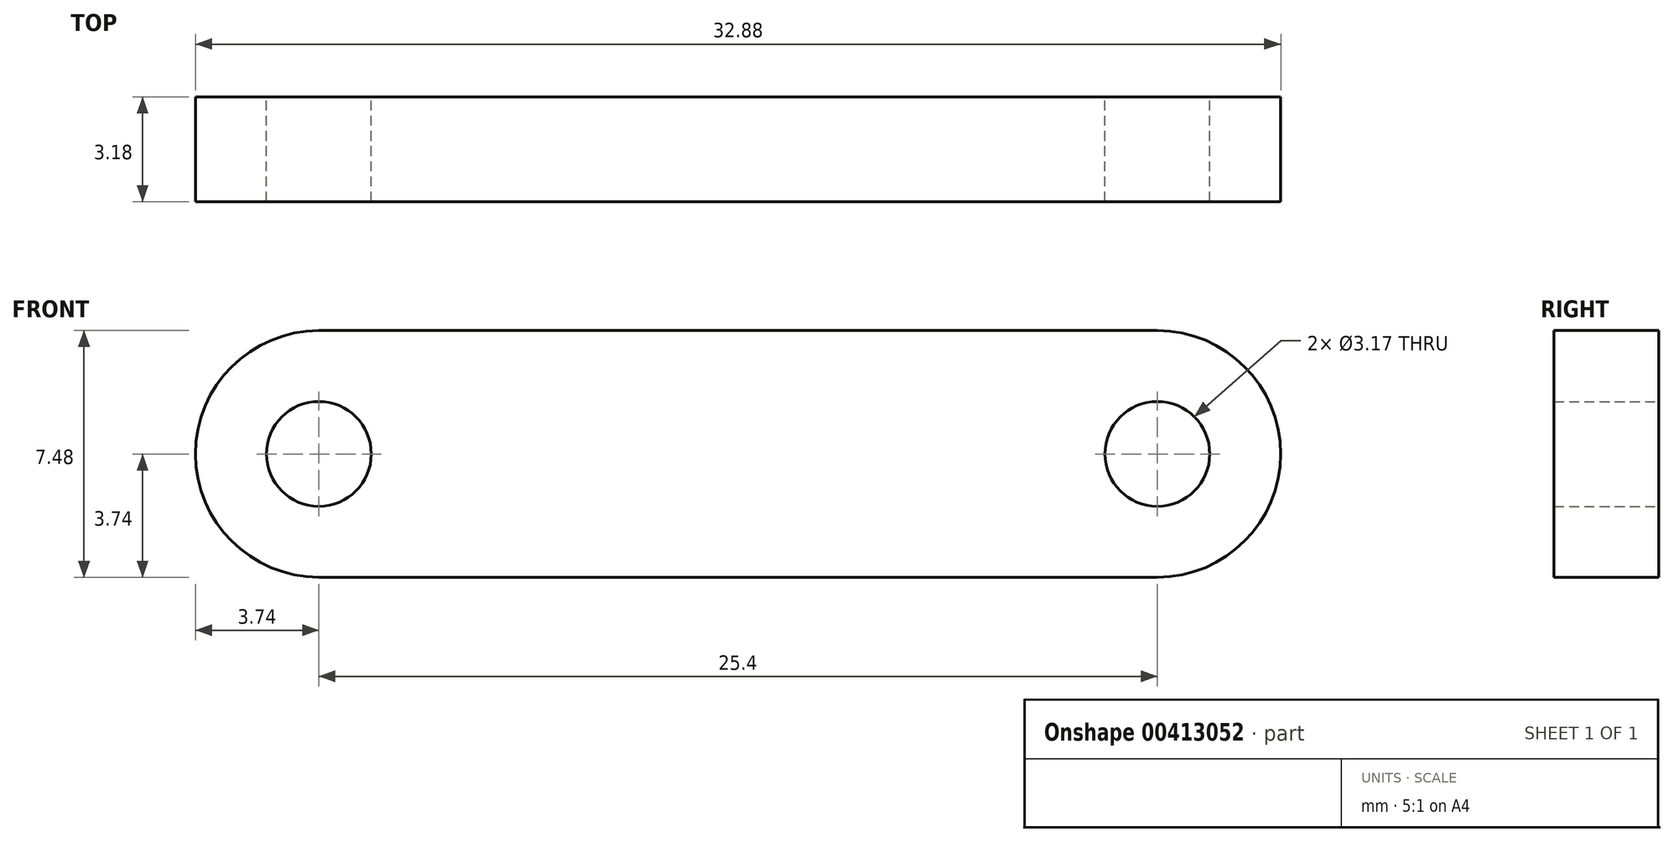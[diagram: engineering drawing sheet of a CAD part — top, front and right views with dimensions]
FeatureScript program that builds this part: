
annotation { "Feature Type Name" : "Feature", "Feature Type Description" : "" }
export const myFeature = defineFeature(function(context is Context, id is Id, definition is map)
    precondition{}
    {
        {
            var Q0;
            Q0=qCreatedBy(makeId("Front.planeOp"),FACE);
            var sketch = newSketch(context, id + "F0", { "sketchPlane" : qUnion([Q0])});
            skCircle(sketch, "E0", {"center": v(0, 0) * mm, "radius": 1.59 * mm});
            skCircle(sketch, "E1", {"center": v(25.4, 0) * mm, "radius": 1.59 * mm});
            skArc(sketch, "E2", {"start": v(0, 3.74) * mm, "mid": v(-3.74, 0) * mm, "end": v(0, -3.74) * mm});
            skArc(sketch, "E3", {"start": v(25.4, -3.74) * mm, "mid": v(29.14, 0) * mm, "end": v(25.4, 3.74) * mm});
            skLineSegment(sketch, "E4", {"start": v(0, 3.74) * mm, "end": v(25.4, 3.74) * mm});
            skLineSegment(sketch, "E5", {"start": v(0, -3.74) * mm, "end": v(25.4, -3.74) * mm});
            skSolve(sketch);
        }
        {
            var Q0;
            Q0 = qSketchRegion(id + "F0", true);
            extrude(context, id + "F1", {"entities" : qUnion([Q0]), "depth" : 3.17 * mm});
        }
    });
